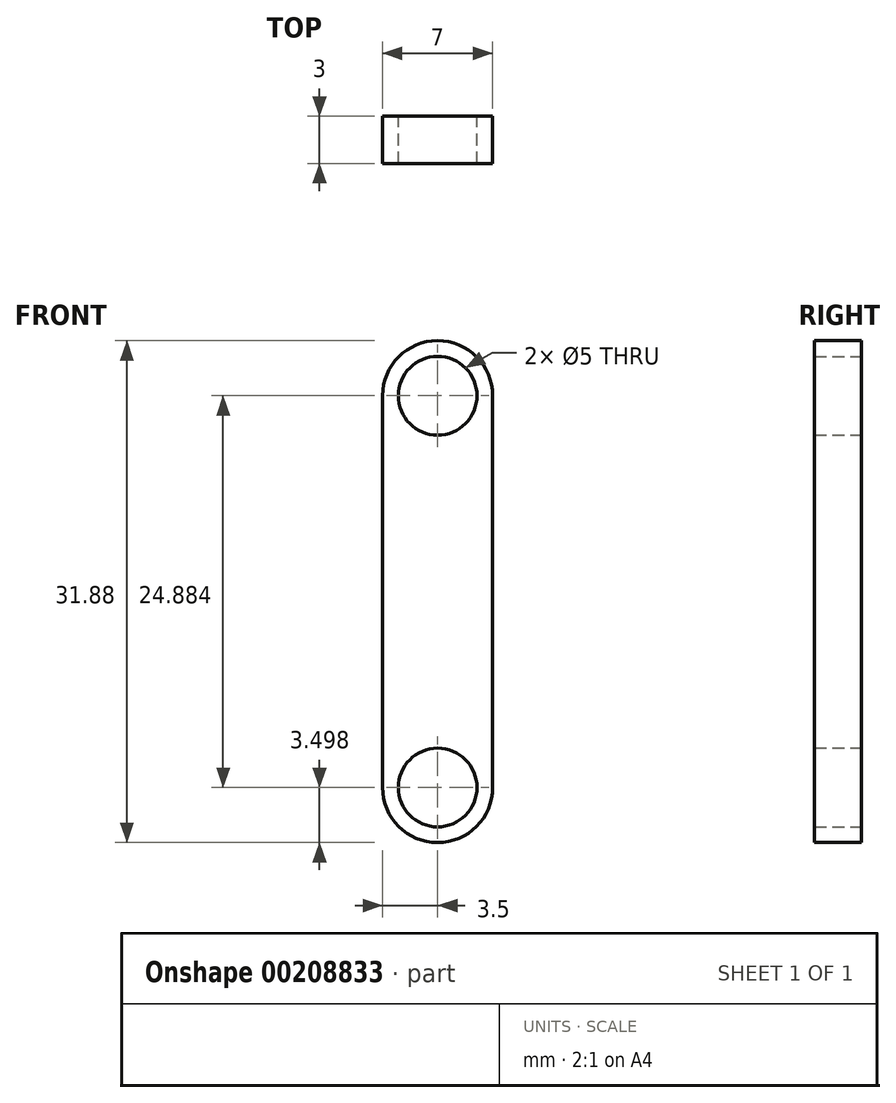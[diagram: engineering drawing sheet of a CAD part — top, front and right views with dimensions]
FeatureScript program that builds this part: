
annotation { "Feature Type Name" : "Feature", "Feature Type Description" : "" }
export const myFeature = defineFeature(function(context is Context, id is Id, definition is map)
    precondition{}
    {
        {
            var Q0;
            Q0=qCreatedBy(makeId("Front.planeOp"),FACE);
            var sketch = newSketch(context, id + "F0", { "sketchPlane" : qUnion([Q0])});
            skArc(sketch, "E0", {"start": v(-2.5, 14.17) * mm, "mid": v(0, 11.67) * mm, "end": v(2.5, 14.17) * mm});
            skArc(sketch, "E1.MirrorCS", {"start": v(-2.5, 39.05) * mm, "mid": v(0, 41.55) * mm, "end": v(2.5, 39.05) * mm});
            skLineSegment(sketch, "E2.0", {"start": v(-3.5, 26.6) * mm, "end": v(-3.5, 39.05) * mm});
            skLineSegment(sketch, "E2.1", {"start": v(3.5, 26.6) * mm, "end": v(3.5, 39.05) * mm});
            skLineSegment(sketch, "E2.2", {"start": v(3.5, 26.6) * mm, "end": v(3.5, 14.17) * mm});
            skArc(sketch, "E2.3", {"start": v(-3.5, 39.05) * mm, "mid": v(0, 42.55) * mm, "end": v(3.5, 39.05) * mm});
            skArc(sketch, "E2.4", {"start": v(-3.5, 14.17) * mm, "mid": v(0, 10.67) * mm, "end": v(3.5, 14.17) * mm});
            skLineSegment(sketch, "E2.5", {"start": v(-3.5, 26.6) * mm, "end": v(-3.5, 14.17) * mm});
            skCircle(sketch, "E3", {"center": v(0, 14.17) * mm, "radius": 2.5 * mm});
            skCircle(sketch, "E4", {"center": v(0, 39.05) * mm, "radius": 2.5 * mm});
            skSolve(sketch);
        }
        {
            var Q0;
            Q0=makeQuery(id+"F0.imprint","IMPRINT",FACE,{"disambiguationData":[TD([[makeQuery(id+"F0.imprint","IMPRINT",EDGE,{"derivedFrom":sQuery(id+"F0.wireOp",EDGE,"E2.0")}),-1.0]])]});
            extrude(context, id + "F1", {"entities" : qUnion([Q0]), "depth" : 3 * mm});
        }
    });
